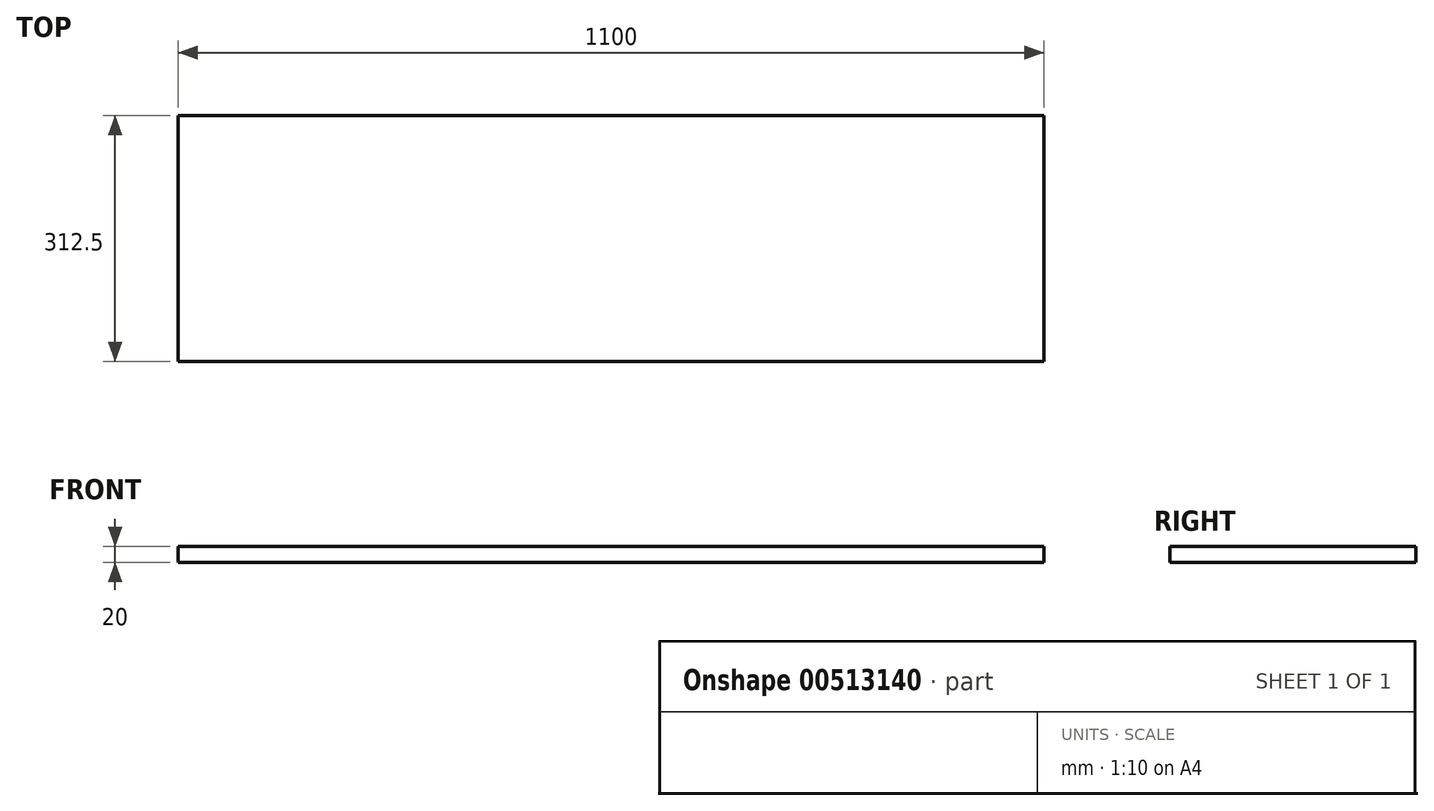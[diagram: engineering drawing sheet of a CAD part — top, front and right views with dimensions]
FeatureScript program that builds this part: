
annotation { "Feature Type Name" : "Feature", "Feature Type Description" : "" }
export const myFeature = defineFeature(function(context is Context, id is Id, definition is map)
    precondition{}
    {
        {
            var Q0;
            Q0=qCreatedBy(makeId("Top.planeOp"),FACE);
            var sketch = newSketch(context, id + "F0", { "sketchPlane" : qUnion([Q0])});
            skLineSegment(sketch, "E0.bottom", {"start": v(550, 156.25) * mm, "end": v(-550, 156.25) * mm});
            skLineSegment(sketch, "E0.top", {"start": v(550, -156.25) * mm, "end": v(-550, -156.25) * mm});
            skLineSegment(sketch, "E0.left", {"start": v(550, 156.25) * mm, "end": v(550, -156.25) * mm});
            skLineSegment(sketch, "E0.right", {"start": v(-550, 156.25) * mm, "end": v(-550, -156.25) * mm});
            skPoint(sketch, "E0.middle", {"position": v(0, 0) * mm});
            skSolve(sketch);
        }
        {
            var Q0;
            Q0=makeQuery(id+"F0.imprint","IMPRINT",FACE,{"disambiguationData":[TD([[makeQuery(id+"F0.imprint","IMPRINT",EDGE,{"derivedFrom":sQuery(id+"F0.wireOp",EDGE,"E0.bottom")}),1.0]])]});
            extrude(context, id + "F1", {"entities" : qUnion([Q0]), "depth" : 20 * mm, "offsetDistance" : 25 * mm});
        }
    });
